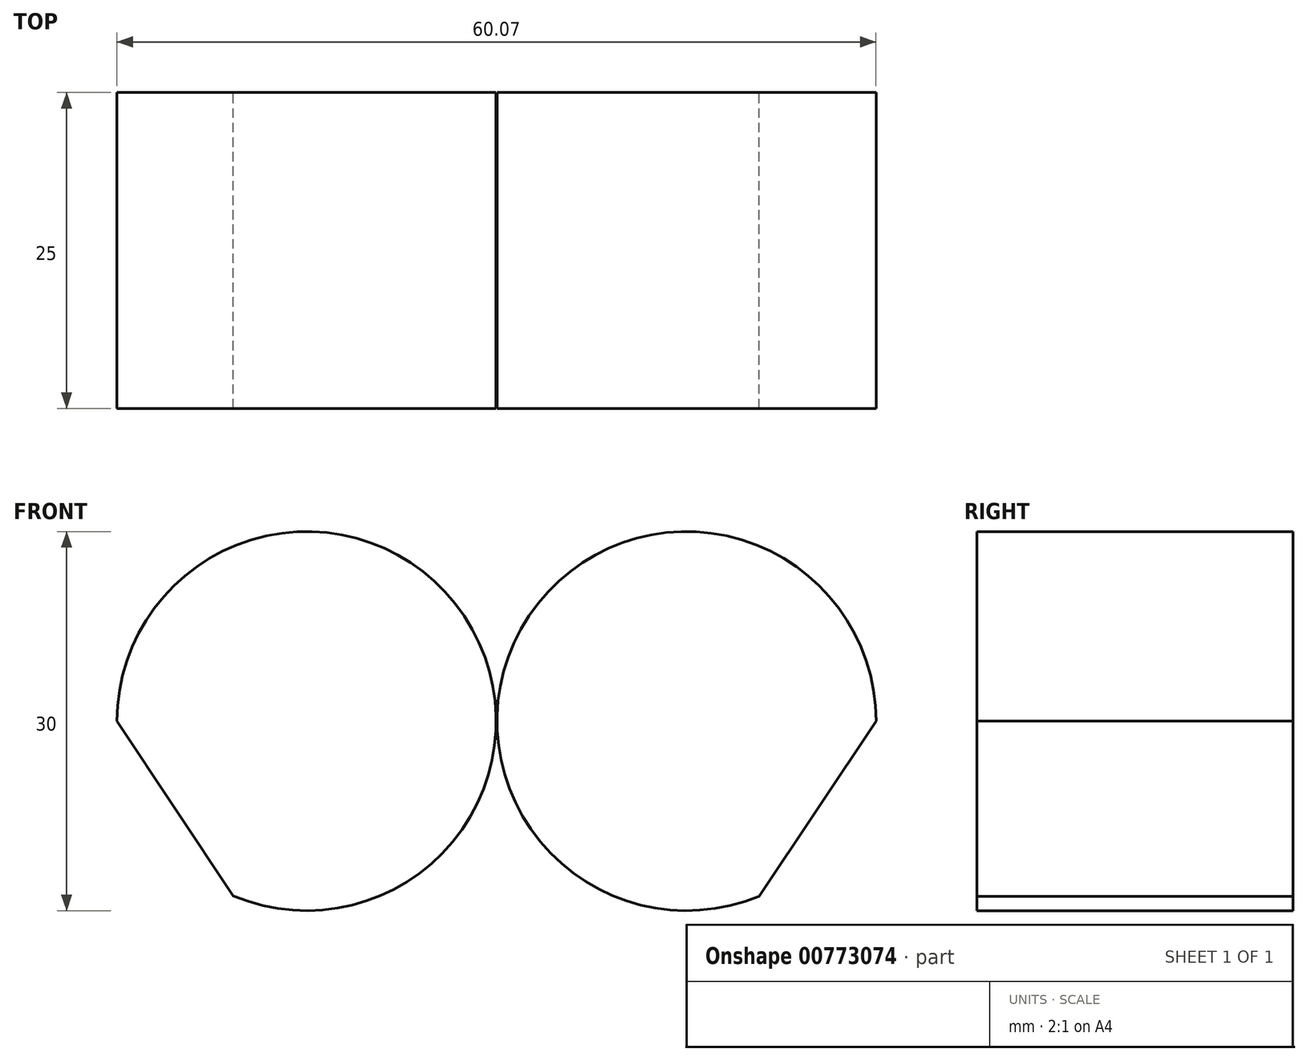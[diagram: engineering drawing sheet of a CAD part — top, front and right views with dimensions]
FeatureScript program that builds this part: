
annotation { "Feature Type Name" : "Feature", "Feature Type Description" : "" }
export const myFeature = defineFeature(function(context is Context, id is Id, definition is map)
    precondition{}
    {
        {
            var Q0;
            Q0=qCreatedBy(makeId("Front.planeOp"),FACE);
            var sketch = newSketch(context, id + "F0", { "sketchPlane" : qUnion([Q0])});
            skArc(sketch, "E0", {"start": v(-20.78, -13.84) * mm, "mid": v(-2.5, 8.31) * mm, "end": v(-30, 0) * mm});
            skArc(sketch, "E1", {"start": v(30.08, 0) * mm, "mid": v(2.6, 8.33) * mm, "end": v(20.84, -13.85) * mm});
            skPoint(sketch, "E2.start.orphan", {"position": v(0, -45.06) * mm});
            skPoint(sketch, "E3.start.orphan", {"position": v(-33.73, 0) * mm});
            skLineSegment(sketch, "E4", {"start": v(-30, 0) * mm, "end": v(0, -45.06) * mm});
            skLineSegment(sketch, "E5", {"start": v(30.08, 0) * mm, "end": v(0, -45.06) * mm});
            skSolve(sketch);
        }
        {
            var Q0;
            Q0 = qSketchRegion(id + "F0", true);
            extrude(context, id + "F1", {"entities" : qUnion([Q0]), "depth" : 25 * mm, "offsetDistance" : 25 * mm});
        }
    });
